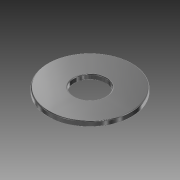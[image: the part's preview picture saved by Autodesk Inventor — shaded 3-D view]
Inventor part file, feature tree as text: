
AUTODESK INVENTOR PART (.ipt)
format: ipt  version: 2013 (Build 170138000, 138)  size: 109,056 bytes
history: native  units: mm
features: other x1, extrude x1, fillet x1, sketch x1
ambient origin geometry x1: Origin
feature tree (4):
  other  "ソリッド1"
  extrude  "押し出し1"  Depth=8.0mm
  fillet  "フィレット1"  Radius=3.0mm
  sketch  "スケッチ1"
